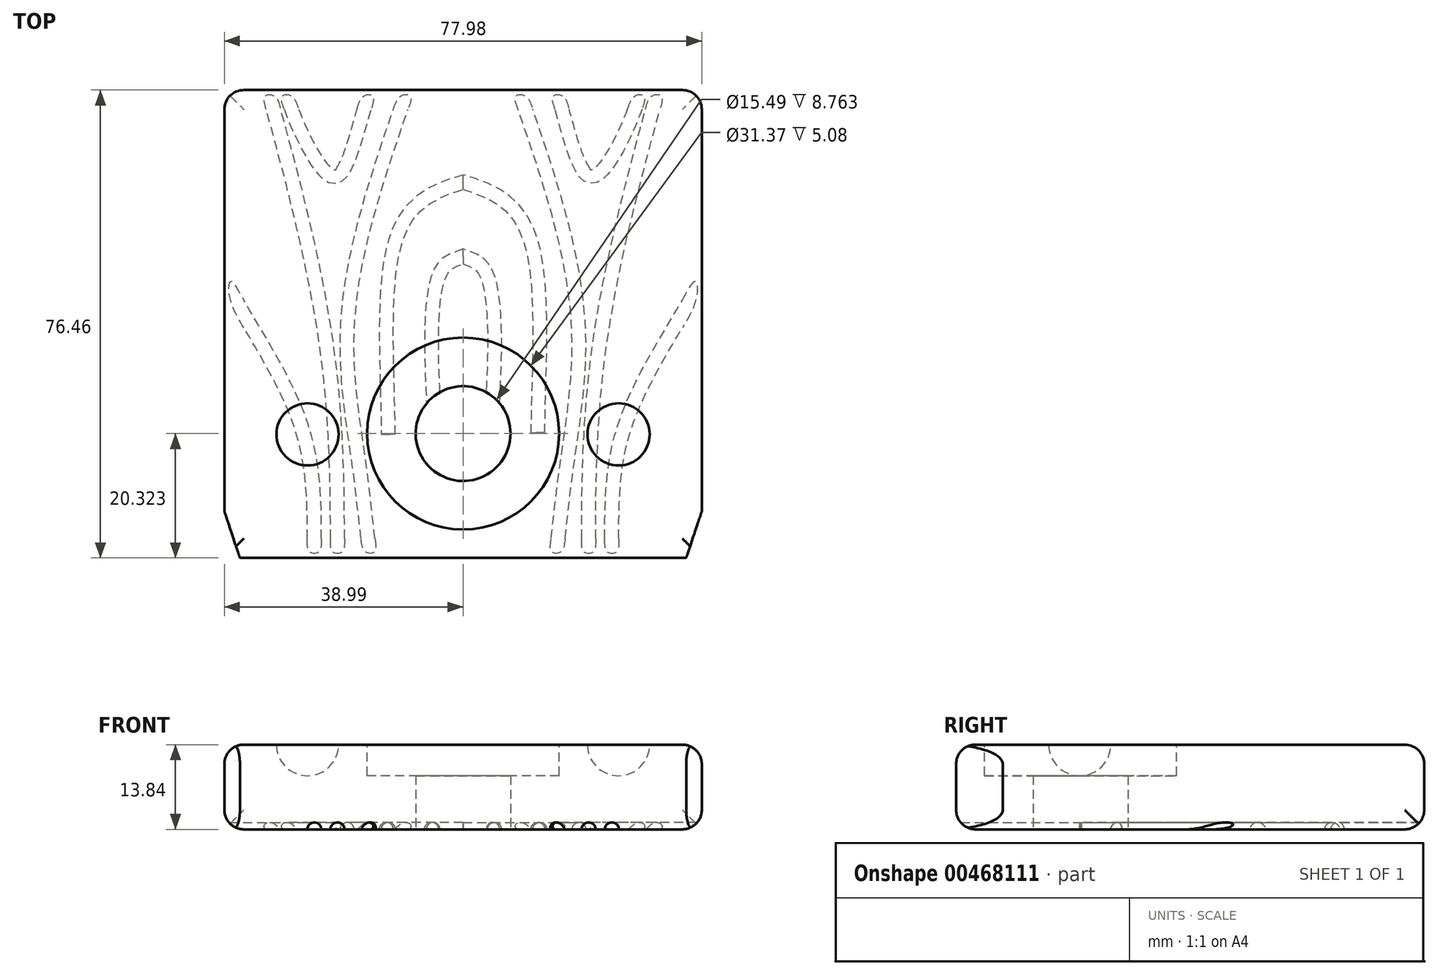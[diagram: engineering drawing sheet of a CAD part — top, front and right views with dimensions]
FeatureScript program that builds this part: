
annotation { "Feature Type Name" : "Feature", "Feature Type Description" : "" }
export const myFeature = defineFeature(function(context is Context, id is Id, definition is map)
    precondition{}
    {
        {
            var Q0;
            Q0=qCreatedBy(makeId("Top.planeOp"),FACE);
            var sketch = newSketch(context, id + "F0", { "sketchPlane" : qUnion([Q0])});
            skLineSegment(sketch, "E0.bottom", {"start": v(38.99, 38.23) * mm, "end": v(-38.99, 38.23) * mm});
            skLineSegment(sketch, "E0.top", {"start": v(38.99, -38.23) * mm, "end": v(-38.99, -38.23) * mm});
            skLineSegment(sketch, "E0.left", {"start": v(38.99, 38.23) * mm, "end": v(38.99, -38.23) * mm});
            skLineSegment(sketch, "E0.right", {"start": v(-38.99, 38.23) * mm, "end": v(-38.99, -38.23) * mm});
            skPoint(sketch, "E0.middle", {"position": v(0, 0) * mm});
            skCircle(sketch, "E1", {"center": v(0, -17.9) * mm, "radius": 7.75 * mm});
            skSolve(sketch);
        }
        {
            var Q0;
            Q0=makeQuery(id+"F0.imprint","IMPRINT",FACE,{"disambiguationData":[TD([[makeQuery(id+"F0.imprint","IMPRINT",EDGE,{"derivedFrom":sQuery(id+"F0.wireOp",EDGE,"E0.bottom")}),1.0]])]});
            extrude(context, id + "F1", {"entities" : qUnion([Q0]), "depth" : 13.84 * mm});
        }
        {
            var Q0;
            Q0=makeQuery(id+"F1.opExtrude","CAP_FACE",FACE,{"disambiguationData":[OSD([sQuery(id+"F0.wireOp",EDGE,"E0.bottom"),sQuery(id+"F0.wireOp",EDGE,"E0.top"),sQuery(id+"F0.wireOp",EDGE,"E0.left"),sQuery(id+"F0.wireOp",EDGE,"E0.right"),sQuery(id+"F0.wireOp",EDGE,"E1")])],"isStart":false});
            var sketch = newSketch(context, id + "F2", { "sketchPlane" : qUnion([Q0])});
            skCircle(sketch, "E2.0", {"center": v(0, -17.9) * mm, "radius": 7.75 * mm});
            skCircle(sketch, "E3", {"center": v(0, -17.9) * mm, "radius": 15.68 * mm});
            skSolve(sketch);
        }
        {
            var Q0;
            Q0=makeQuery(id+"F2.imprint","IMPRINT",FACE,{"disambiguationData":[TD([[makeQuery(id+"F2.imprint","IMPRINT",EDGE,{"derivedFrom":sQuery(id+"F2.wireOp",EDGE,"E2.0")}),-1.0]])]});
            extrude(context, id + "F3", {"entities" : qUnion([Q0]), "operationType" : NewBodyOperationType.REMOVE, "oppositeDirection" : true, "depth" : 5.08 * mm});
        }
        {
            var Q0;
            Q0=qCreatedBy(makeId("Front.planeOp"),FACE);
            cPlane(context, id + "F4", {"entities" : qUnion([Q0]), "cplaneType" : CPlaneType.OFFSET, "offset" : 18.03 * mm, "width" : 152.4 * mm, "height" : 152.4 * mm});
        }
        {
            var Q0;
            Q0=qCreatedBy(id+"F4.planeOp",FACE);
            var sketch = newSketch(context, id + "F5", { "sketchPlane" : qUnion([Q0])});
            skLineSegment(sketch, "E4.0", {"start": v(38.99, 13.84) * mm, "end": v(-38.99, 13.84) * mm});
            skArc(sketch, "E5", {"start": v(-30.48, 13.84) * mm, "mid": v(-25.4, 8.76) * mm, "end": v(-20.32, 13.84) * mm});
            skArc(sketch, "E6.MirrorCS", {"start": v(30.48, 13.84) * mm, "mid": v(25.4, 8.76) * mm, "end": v(20.32, 13.84) * mm});
            skSolve(sketch);
        }
        {
            var Q0;
            Q0 = qSketchRegion(id + "F5", true);
            var Q1;
            Q1=sQuery(id+"F5.wireOp",EDGE,"E4.0");
            revolve(context, id + "F6", {"operationType" : NewBodyOperationType.REMOVE, "entities" : qUnion([Q0]), "axis" : qUnion([Q1]), "revolveType" : RevolveType.FULL, "oppositeDirection" : true});
        }
        {
            var Q0;
            Q0=makeQuery(id+"F1.opExtrude","SWEPT_EDGE",EDGE,{"disambiguationData":[OSD([sQuery(id+"F0.wireOp",EDGE,"E0.top"),sQuery(id+"F0.wireOp",EDGE,"E0.right")])]});
            var Q1;
            Q1=makeQuery(id+"F1.opExtrude","SWEPT_EDGE",EDGE,{"disambiguationData":[OSD([sQuery(id+"F0.wireOp",EDGE,"E0.top"),sQuery(id+"F0.wireOp",EDGE,"E0.left")])]});
            chamfer(context, id + "F7", {"entities" : qUnion([Q0, Q1]), "chamferType" : ChamferType.TWO_OFFSETS, "width1" : 2.54 * mm, "oppositeDirection" : false, "width2" : 7.62 * mm});
        }
        {
            var Q0;
            Q0=qCreatedBy(makeId("Top.planeOp"),FACE);
            var sketch = newSketch(context, id + "F8", { "sketchPlane" : qUnion([Q0])});
            skPoint(sketch, "E7.0", {"position": v(-35.81, 0) * mm});
            skFitSpline(sketch, "E8", {"points": [v(39.06, 7.42) * mm, v(26.22, -17.3) * mm, v(24.29, -38.04) * mm], "startDerivative": vector(-21.66, -42.08) * mm, "endDerivative": vector(-0.35, -37.77) * mm});
            skFitSpline(sketch, "E9", {"points": [v(31.84, 38.23) * mm, v(22.23, -3.88) * mm, v(20.51, -38.04) * mm], "startDerivative": vector(-20.67, -75.16) * mm, "endDerivative": vector(0.12, -64.83) * mm});
            skFitSpline(sketch, "E10", {"points": [v(29, 38.23) * mm, v(24.75, 28) * mm, v(20.51, 24.22) * mm, v(15.1, 38.57) * mm], "startDerivative": vector(-5.15, -22.25) * mm, "endDerivative": vector(-13.12, 38.58) * mm});
            skFitSpline(sketch, "E11", {"points": [v(9.07, 38.17) * mm, v(18.67, 2.2) * mm, v(16.88, -23.38) * mm, v(15.1, -38.04) * mm], "startDerivative": vector(28.46, -81.14) * mm, "endDerivative": vector(-6.65, -43.93) * mm});
            skFitSpline(sketch, "E12", {"points": [v(12.22, -17.9) * mm, v(11.95, 9.33) * mm, v(7.13, 19.82) * mm, v(0, 23.17) * mm], "startDerivative": vector(-0.09, 43.18) * mm, "endDerivative": vector(-28.23, 8.15) * mm});
            skFitSpline(sketch, "E13", {"points": [v(4.57, -17.9) * mm, v(3.78, 8.28) * mm, v(0, 11.01) * mm], "startDerivative": vector(0.77, 22.83) * mm, "endDerivative": vector(-11.34, 4.74) * mm});
            skFitSpline(sketch, "E14.MirrorCS", {"points": [v(-4.57, -17.9) * mm, v(-3.78, 8.28) * mm, v(0, 11.01) * mm], "startDerivative": vector(-0.77, 22.83) * mm, "endDerivative": vector(11.34, 4.74) * mm});
            skFitSpline(sketch, "E15.MirrorCS", {"points": [v(-12.22, -17.9) * mm, v(-11.95, 9.33) * mm, v(-7.13, 19.82) * mm, v(0, 23.17) * mm], "startDerivative": vector(0.09, 43.18) * mm, "endDerivative": vector(28.23, 8.15) * mm});
            skFitSpline(sketch, "E16.MirrorCS", {"points": [v(-9.07, 38.17) * mm, v(-18.67, 2.2) * mm, v(-16.88, -23.38) * mm, v(-15.1, -38.04) * mm], "startDerivative": vector(-28.46, -81.14) * mm, "endDerivative": vector(6.65, -43.93) * mm});
            skFitSpline(sketch, "E17.MirrorCS", {"points": [v(-29, 38.23) * mm, v(-24.75, 28) * mm, v(-20.51, 24.22) * mm, v(-15.1, 38.57) * mm], "startDerivative": vector(5.15, -22.25) * mm, "endDerivative": vector(13.12, 38.58) * mm});
            skFitSpline(sketch, "E18.MirrorCS", {"points": [v(-31.84, 38.23) * mm, v(-22.23, -3.88) * mm, v(-20.51, -38.04) * mm], "startDerivative": vector(20.67, -75.16) * mm, "endDerivative": vector(-0.12, -64.83) * mm});
            skFitSpline(sketch, "E19.MirrorCS", {"points": [v(-39.06, 7.42) * mm, v(-26.22, -17.3) * mm, v(-24.29, -38.04) * mm], "startDerivative": vector(21.66, -42.08) * mm, "endDerivative": vector(0.35, -37.77) * mm});
            skLineSegment(sketch, "E20.0", {"start": v(38.99, 38.23) * mm, "end": v(-38.99, 38.23) * mm});
            skLineSegment(sketch, "E21.0", {"start": v(38.99, 38.23) * mm, "end": v(38.99, -30.6) * mm});
            skLineSegment(sketch, "E22.0", {"start": v(-38.99, 38.23) * mm, "end": v(-38.99, -30.6) * mm});
            skLineSegment(sketch, "E23.0", {"start": v(36.45, -38.23) * mm, "end": v(-36.45, -38.23) * mm});
            skCircle(sketch, "E24.0", {"center": v(0, -17.9) * mm, "radius": 7.75 * mm});
            skLineSegment(sketch, "E25", {"start": v(48.87, -17.9) * mm, "end": v(-50.84, -17.9) * mm, "construction": true});
            skLineSegment(sketch, "E26.0.2", {"start": v(-38.99, 38.23) * mm, "end": v(38.99, 38.23) * mm});
            skLineSegment(sketch, "E27", {"start": v(-37.89, 38.23) * mm, "end": v(38.99, 38.23) * mm});
            skSolve(sketch);
        }
        {
            var Q0;
            Q0=makeQuery(id+"F1.opExtrude","SWEPT_FACE",FACE,{"disambiguationData":[OSD([sQuery(id+"F0.wireOp",EDGE,"E0.top")])]});
            var sketch = newSketch(context, id + "F9", { "sketchPlane" : qUnion([Q0])});
            skPoint(sketch, "E28.0", {"position": v(24.29, 0) * mm});
            skPoint(sketch, "E29.0", {"position": v(15.1, 0) * mm});
            skPoint(sketch, "E30.0", {"position": v(-15.1, 0) * mm});
            skPoint(sketch, "E31.0", {"position": v(-20.51, 0) * mm});
            skPoint(sketch, "E32.0", {"position": v(-24.29, 0) * mm});
            skPoint(sketch, "E33.0", {"position": v(20.51, 0) * mm});
            skCircle(sketch, "E34", {"center": v(24.29, 0) * mm, "radius": 1.14 * mm});
            skCircle(sketch, "E35", {"center": v(20.51, 0) * mm, "radius": 1.14 * mm});
            skCircle(sketch, "E36", {"center": v(15.1, 0) * mm, "radius": 1.14 * mm});
            skCircle(sketch, "E37", {"center": v(-15.1, 0) * mm, "radius": 1.14 * mm});
            skCircle(sketch, "E38", {"center": v(-20.51, 0) * mm, "radius": 1.14 * mm});
            skCircle(sketch, "E39", {"center": v(-24.29, 0) * mm, "radius": 1.14 * mm});
            skSolve(sketch);
        }
        {
            var Q0;
            {var subQ0=sQuery(id+"F9.wireOp",EDGE,"E34");var subQ1=makeQuery(id+"F1.opExtrude","CAP_EDGE",EDGE,{"disambiguationData":[OSD([sQuery(id+"F0.wireOp",EDGE,"E0.top")])],"isStart":true});var subQ2=makeQuery(id+"F9.imprint","INTERSECT",VERTEX,{"disambiguationData":[OD(0.0)],"derivedFrom":[subQ1,subQ0]});Q0=makeQuery(id+"F9.imprint","IMPRINT",FACE,{"disambiguationData":[TD([[makeQuery(id+"F9.imprint","IMPRINT",EDGE,{"disambiguationData":[TD([[subQ2,-1.0]])],"derivedFrom":subQ0}),1.0]])]});}
            var Q1;
            Q1=sQuery(id+"F8.wireOp",EDGE,"E8");
            sweep(context, id + "F10", {"operationType" : NewBodyOperationType.REMOVE, "profiles" : qUnion([Q0]), "path" : qUnion([Q1])});
        }
        {
            var Q0;
            {var subQ0=sQuery(id+"F9.wireOp",EDGE,"E35");var subQ1=makeQuery(id+"F1.opExtrude","CAP_EDGE",EDGE,{"disambiguationData":[OSD([sQuery(id+"F0.wireOp",EDGE,"E0.top")])],"isStart":true});var subQ2=makeQuery(id+"F9.imprint","INTERSECT",VERTEX,{"disambiguationData":[OD(0.0)],"derivedFrom":[subQ1,subQ0]});Q0=makeQuery(id+"F9.imprint","IMPRINT",FACE,{"disambiguationData":[TD([[makeQuery(id+"F9.imprint","IMPRINT",EDGE,{"disambiguationData":[TD([[subQ2,-1.0]])],"derivedFrom":subQ0}),1.0]])]});}
            var Q1;
            Q1=sQuery(id+"F8.wireOp",EDGE,"E9");
            sweep(context, id + "F11", {"operationType" : NewBodyOperationType.REMOVE, "profiles" : qUnion([Q0]), "path" : qUnion([Q1])});
        }
        {
            var Q0;
            {var subQ0=sQuery(id+"F9.wireOp",EDGE,"E36");var subQ1=makeQuery(id+"F1.opExtrude","CAP_EDGE",EDGE,{"disambiguationData":[OSD([sQuery(id+"F0.wireOp",EDGE,"E0.top")])],"isStart":true});var subQ2=makeQuery(id+"F9.imprint","INTERSECT",VERTEX,{"disambiguationData":[OD(0.0)],"derivedFrom":[subQ1,subQ0]});Q0=makeQuery(id+"F9.imprint","IMPRINT",FACE,{"disambiguationData":[TD([[makeQuery(id+"F9.imprint","IMPRINT",EDGE,{"disambiguationData":[TD([[subQ2,-1.0]])],"derivedFrom":subQ0}),1.0]])]});}
            var Q1;
            Q1=sQuery(id+"F8.wireOp",EDGE,"E11");
            sweep(context, id + "F12", {"operationType" : NewBodyOperationType.REMOVE, "profiles" : qUnion([Q0]), "path" : qUnion([Q1])});
        }
        {
            var Q0;
            {var subQ0=sQuery(id+"F9.wireOp",EDGE,"E37");var subQ1=makeQuery(id+"F1.opExtrude","CAP_EDGE",EDGE,{"disambiguationData":[OSD([sQuery(id+"F0.wireOp",EDGE,"E0.top")])],"isStart":true});var subQ2=makeQuery(id+"F9.imprint","INTERSECT",VERTEX,{"disambiguationData":[OD(0.0)],"derivedFrom":[subQ1,subQ0]});Q0=makeQuery(id+"F9.imprint","IMPRINT",FACE,{"disambiguationData":[TD([[makeQuery(id+"F9.imprint","IMPRINT",EDGE,{"disambiguationData":[TD([[subQ2,1.0]])],"derivedFrom":subQ0}),1.0]])]});}
            var Q1;
            Q1=sQuery(id+"F8.wireOp",EDGE,"E16.MirrorCS");
            sweep(context, id + "F13", {"operationType" : NewBodyOperationType.REMOVE, "profiles" : qUnion([Q0]), "path" : qUnion([Q1])});
        }
        {
            var Q0;
            {var subQ0=sQuery(id+"F9.wireOp",EDGE,"E38");var subQ1=makeQuery(id+"F1.opExtrude","CAP_EDGE",EDGE,{"disambiguationData":[OSD([sQuery(id+"F0.wireOp",EDGE,"E0.top")])],"isStart":true});var subQ2=makeQuery(id+"F9.imprint","INTERSECT",VERTEX,{"disambiguationData":[OD(0.0)],"derivedFrom":[subQ1,subQ0]});Q0=makeQuery(id+"F9.imprint","IMPRINT",FACE,{"disambiguationData":[TD([[makeQuery(id+"F9.imprint","IMPRINT",EDGE,{"disambiguationData":[TD([[subQ2,1.0]])],"derivedFrom":subQ0}),1.0]])]});}
            var Q1;
            Q1=sQuery(id+"F8.wireOp",EDGE,"E18.MirrorCS");
            sweep(context, id + "F14", {"operationType" : NewBodyOperationType.REMOVE, "profiles" : qUnion([Q0]), "path" : qUnion([Q1])});
        }
        {
            var Q0;
            {var subQ0=sQuery(id+"F9.wireOp",EDGE,"E39");var subQ1=makeQuery(id+"F1.opExtrude","CAP_EDGE",EDGE,{"disambiguationData":[OSD([sQuery(id+"F0.wireOp",EDGE,"E0.top")])],"isStart":true});var subQ2=makeQuery(id+"F9.imprint","INTERSECT",VERTEX,{"disambiguationData":[OD(0.0)],"derivedFrom":[subQ1,subQ0]});Q0=makeQuery(id+"F9.imprint","IMPRINT",FACE,{"disambiguationData":[TD([[makeQuery(id+"F9.imprint","IMPRINT",EDGE,{"disambiguationData":[TD([[subQ2,1.0]])],"derivedFrom":subQ0}),1.0]])]});}
            var Q1;
            Q1=sQuery(id+"F8.wireOp",EDGE,"E19.MirrorCS");
            sweep(context, id + "F15", {"operationType" : NewBodyOperationType.REMOVE, "profiles" : qUnion([Q0]), "path" : qUnion([Q1])});
        }
        {
            var Q0;
            Q0=makeQuery(id+"F1.opExtrude","SWEPT_FACE",FACE,{"disambiguationData":[OSD([sQuery(id+"F0.wireOp",EDGE,"E0.bottom")])]});
            var sketch = newSketch(context, id + "F16", { "sketchPlane" : qUnion([Q0])});
            skPoint(sketch, "E40.0", {"position": v(15.22, 0) * mm});
            skPoint(sketch, "E41.0", {"position": v(-15.1, 0) * mm});
            skCircle(sketch, "E42", {"center": v(15.22, 0) * mm, "radius": 1.14 * mm});
            skCircle(sketch, "E43", {"center": v(-15.1, 0) * mm, "radius": 1.14 * mm});
            skPoint(sketch, "E44.0", {"position": v(29, 0) * mm});
            skPoint(sketch, "E45.0", {"position": v(-29, 0) * mm});
            skCircle(sketch, "E46", {"center": v(-29, 0) * mm, "radius": 1.14 * mm});
            skCircle(sketch, "E47", {"center": v(29, 0) * mm, "radius": 1.14 * mm});
            skSolve(sketch);
        }
        {
            var Q0;
            {var subQ0=sQuery(id+"F16.wireOp",EDGE,"E47");var subQ1=sQuery(id+"F0.wireOp",EDGE,"E0.bottom");var subQ3=sQuery(id+"F0.wireOp",EDGE,"E0.right");var subQ6=makeQuery(id+"F13.opSweep","SWEPT_FACE",FACE,{"disambiguationData":[OSD([sQuery(id+"F8.wireOp",EDGE,"E16.MirrorCS"),sQuery(id+"F9.wireOp",EDGE,"E37")])]});var subQ7=makeQuery(id+"F1.opExtrude","SWEPT_FACE",FACE,{"disambiguationData":[OSD([subQ3])]});var subQ8=makeQuery(id+"F14.boolean.opBoolean","SPLIT",EDGE,{"disambiguationData":[TD([makeQuery(id+"F13.boolean.opBoolean","COPY",FACE,{"derivedFrom":subQ6})])],"derivedFrom":makeQuery(id+"F13.boolean.opBoolean","SPLIT",EDGE,{"disambiguationData":[TD([subQ7])],"derivedFrom":makeQuery(id+"F12.boolean.opBoolean","SPLIT",EDGE,{"disambiguationData":[TD([subQ7])],"derivedFrom":makeQuery(id+"F11.boolean.opBoolean","SPLIT",EDGE,{"disambiguationData":[TD([subQ7])],"derivedFrom":makeQuery(id+"F1.opExtrude","CAP_EDGE",EDGE,{"disambiguationData":[OSD([subQ1])],"isStart":true})})})})});var subQ9=makeQuery(id+"F16.imprint","INTERSECT",VERTEX,{"disambiguationData":[OD(0.0)],"derivedFrom":[subQ8,subQ0]});Q0=makeQuery(id+"F16.imprint","IMPRINT",FACE,{"disambiguationData":[TD([[makeQuery(id+"F16.imprint","IMPRINT",EDGE,{"disambiguationData":[TD([[subQ9,-1.0]])],"derivedFrom":subQ0}),1.0]])]});}
            var Q1;
            Q1=sQuery(id+"F8.wireOp",EDGE,"E17.MirrorCS");
            sweep(context, id + "F17", {"operationType" : NewBodyOperationType.REMOVE, "profiles" : qUnion([Q0]), "path" : qUnion([Q1])});
        }
        {
            var Q0;
            {var subQ0=sQuery(id+"F16.wireOp",EDGE,"E46");var subQ1=sQuery(id+"F0.wireOp",EDGE,"E0.bottom");var subQ3=sQuery(id+"F0.wireOp",EDGE,"E0.right");var subQ5=makeQuery(id+"F11.opSweep","SWEPT_FACE",FACE,{"disambiguationData":[OSD([sQuery(id+"F8.wireOp",EDGE,"E9"),sQuery(id+"F9.wireOp",EDGE,"E35")])]});var subQ6=makeQuery(id+"F12.boolean.opBoolean","SPLIT",EDGE,{"disambiguationData":[TD([makeQuery(id+"F11.boolean.opBoolean","COPY",FACE,{"derivedFrom":subQ5})])],"derivedFrom":makeQuery(id+"F11.boolean.opBoolean","SPLIT",EDGE,{"disambiguationData":[TD([makeQuery(id+"F1.opExtrude","SWEPT_FACE",FACE,{"disambiguationData":[OSD([subQ3])]})])],"derivedFrom":makeQuery(id+"F1.opExtrude","CAP_EDGE",EDGE,{"disambiguationData":[OSD([subQ1])],"isStart":true})})});var subQ7=makeQuery(id+"F16.imprint","INTERSECT",VERTEX,{"disambiguationData":[OD(0.0)],"derivedFrom":[subQ6,subQ0]});Q0=makeQuery(id+"F16.imprint","IMPRINT",FACE,{"disambiguationData":[TD([[makeQuery(id+"F16.imprint","IMPRINT",EDGE,{"disambiguationData":[TD([[subQ7,1.0]])],"derivedFrom":subQ0}),1.0]])]});}
            var Q1;
            Q1=sQuery(id+"F8.wireOp",EDGE,"E10");
            sweep(context, id + "F18", {"operationType" : NewBodyOperationType.REMOVE, "profiles" : qUnion([Q0]), "path" : qUnion([Q1])});
        }
        {
            var Q0;
            Q0=qCreatedBy(id+"F4.planeOp",FACE);
            var sketch = newSketch(context, id + "F19", { "sketchPlane" : qUnion([Q0])});
            skCircle(sketch, "E48", {"center": v(-12.22, 0) * mm, "radius": 1.14 * mm});
            skCircle(sketch, "E49", {"center": v(-4.58, 0) * mm, "radius": 1.14 * mm});
            skSolve(sketch);
        }
        {
            var Q0;
            Q0=makeQuery(id+"F19.imprint","IMPRINT",FACE,{"disambiguationData":[TD([[makeQuery(id+"F19.imprint","IMPRINT",EDGE,{"derivedFrom":sQuery(id+"F19.wireOp",EDGE,"E48")}),1.0]])]});
            var Q1;
            Q1=sQuery(id+"F8.wireOp",EDGE,"E15.MirrorCS");
            var Q2;
            Q2=sQuery(id+"F8.wireOp",EDGE,"E12");
            sweep(context, id + "F20", {"operationType" : NewBodyOperationType.REMOVE, "profiles" : qUnion([Q0]), "path" : qUnion([Q1, Q2])});
        }
        {
            var Q0;
            Q0=makeQuery(id+"F19.imprint","IMPRINT",FACE,{"disambiguationData":[TD([[makeQuery(id+"F19.imprint","IMPRINT",EDGE,{"derivedFrom":sQuery(id+"F19.wireOp",EDGE,"E49")}),1.0]])]});
            var Q1;
            Q1=sQuery(id+"F8.wireOp",EDGE,"E14.MirrorCS");
            var Q2;
            Q2=sQuery(id+"F8.wireOp",EDGE,"E13");
            sweep(context, id + "F21", {"operationType" : NewBodyOperationType.REMOVE, "profiles" : qUnion([Q0]), "path" : qUnion([Q1, Q2])});
        }
        {
            var Q0;
            Q0=qCreatedBy(makeId("Top.planeOp"),FACE);
            cPlane(context, id + "F22", {"entities" : qUnion([Q0]), "cplaneType" : CPlaneType.OFFSET, "offset" : 6.92 * mm, "width" : 152.4 * mm, "height" : 152.4 * mm});
        }
        {
            var Q0;
            {var subQ0=sQuery(id+"F0.wireOp",EDGE,"E0.right");var subQ1=sQuery(id+"F0.wireOp",EDGE,"E0.top");var subQ4=makeQuery(id+"FcEpPnPIbSgFIcs_1.1.F12.opSweep","SWEPT_FACE",FACE,{"disambiguationData":[OSD([sQuery(id+"F8.wireOp",EDGE,"E11"),sQuery(id+"F9.wireOp",EDGE,"E36")])]});var subQ5=makeQuery(id+"F7.opChamfer","BLEND_FACE",FACE,{"disambiguationData":[OSD([subQ1,subQ0])]});Q0=makeQuery(id+"FcEpPnPIbSgFIcs_1.1.F13.boolean.opBoolean","SPLIT",EDGE,{"disambiguationData":[TD([makeQuery(id+"FcEpPnPIbSgFIcs_1.1.F12.boolean.opBoolean","COPY",FACE,{"derivedFrom":subQ4})])],"derivedFrom":makeQuery(id+"FcEpPnPIbSgFIcs_1.1.F12.boolean.opBoolean","SPLIT",EDGE,{"disambiguationData":[TD([subQ5])],"derivedFrom":makeQuery(id+"FcEpPnPIbSgFIcs_1.1.F11.boolean.opBoolean","SPLIT",EDGE,{"disambiguationData":[TD([subQ5])],"derivedFrom":makeQuery(id+"FcEpPnPIbSgFIcs_1.1.F10.boolean.opBoolean","SPLIT",EDGE,{"disambiguationData":[TD([subQ5])],"derivedFrom":makeQuery(id+"F1.opExtrude","CAP_EDGE",EDGE,{"disambiguationData":[OSD([subQ1])],"isStart":false})})})})});}
            var Q1;
            {var subQ0=sQuery(id+"F0.wireOp",EDGE,"E0.right");var subQ1=sQuery(id+"F0.wireOp",EDGE,"E0.top");var subQ3=makeQuery(id+"F12.opSweep","SWEPT_FACE",FACE,{"disambiguationData":[OSD([sQuery(id+"F8.wireOp",EDGE,"E11"),sQuery(id+"F9.wireOp",EDGE,"E36")])]});var subQ5=makeQuery(id+"F7.opChamfer","BLEND_FACE",FACE,{"disambiguationData":[OSD([subQ1,subQ0])]});Q1=makeQuery(id+"F13.boolean.opBoolean","SPLIT",EDGE,{"disambiguationData":[TD([makeQuery(id+"F12.boolean.opBoolean","COPY",FACE,{"derivedFrom":subQ3})])],"derivedFrom":makeQuery(id+"F12.boolean.opBoolean","SPLIT",EDGE,{"disambiguationData":[TD([subQ5])],"derivedFrom":makeQuery(id+"F11.boolean.opBoolean","SPLIT",EDGE,{"disambiguationData":[TD([subQ5])],"derivedFrom":makeQuery(id+"F10.boolean.opBoolean","SPLIT",EDGE,{"disambiguationData":[TD([subQ5])],"derivedFrom":makeQuery(id+"F1.opExtrude","CAP_EDGE",EDGE,{"disambiguationData":[OSD([subQ1])],"isStart":true})})})})});}
            var Q2;
            Q2=makeQuery(id+"F1.opExtrude","SWEPT_EDGE",EDGE,{"disambiguationData":[OSD([sQuery(id+"F0.wireOp",EDGE,"E0.bottom"),sQuery(id+"F0.wireOp",EDGE,"E0.left")])]});
            var Q3;
            Q3=makeQuery(id+"F1.opExtrude","SWEPT_EDGE",EDGE,{"disambiguationData":[OSD([sQuery(id+"F0.wireOp",EDGE,"E0.bottom"),sQuery(id+"F0.wireOp",EDGE,"E0.right")])]});
            var Q4;
            {var subQ0=sQuery(id+"F0.wireOp",EDGE,"E0.bottom");var subQ2=sQuery(id+"F0.wireOp",EDGE,"E0.left");Q4=makeQuery(id+"FcEpPnPIbSgFIcs_1.1.F10.boolean.opBoolean","SPLIT",EDGE,{"disambiguationData":[TD([makeQuery(id+"F1.opExtrude","SWEPT_FACE",FACE,{"disambiguationData":[OSD([subQ0])]})])],"derivedFrom":makeQuery(id+"F1.opExtrude","CAP_EDGE",EDGE,{"disambiguationData":[OSD([subQ2])],"isStart":false})});}
            var Q5;
            {var subQ0=sQuery(id+"F0.wireOp",EDGE,"E0.bottom");var subQ1=sQuery(id+"F0.wireOp",EDGE,"E0.right");Q5=makeQuery(id+"FcEpPnPIbSgFIcs_1.1.F15.boolean.opBoolean","SPLIT",EDGE,{"disambiguationData":[TD([makeQuery(id+"F1.opExtrude","SWEPT_FACE",FACE,{"disambiguationData":[OSD([subQ0])]})])],"derivedFrom":makeQuery(id+"F1.opExtrude","CAP_EDGE",EDGE,{"disambiguationData":[OSD([subQ1])],"isStart":false})});}
            var Q6;
            {var subQ0=sQuery(id+"F0.wireOp",EDGE,"E0.bottom");var subQ2=sQuery(id+"F0.wireOp",EDGE,"E0.left");Q6=makeQuery(id+"F10.boolean.opBoolean","SPLIT",EDGE,{"disambiguationData":[TD([makeQuery(id+"F1.opExtrude","SWEPT_FACE",FACE,{"disambiguationData":[OSD([subQ0])]})])],"derivedFrom":makeQuery(id+"F1.opExtrude","CAP_EDGE",EDGE,{"disambiguationData":[OSD([subQ2])],"isStart":true})});}
            var Q7;
            {var subQ0=sQuery(id+"F0.wireOp",EDGE,"E0.bottom");var subQ1=sQuery(id+"F0.wireOp",EDGE,"E0.right");Q7=makeQuery(id+"F15.boolean.opBoolean","SPLIT",EDGE,{"disambiguationData":[TD([makeQuery(id+"F1.opExtrude","SWEPT_FACE",FACE,{"disambiguationData":[OSD([subQ0])]})])],"derivedFrom":makeQuery(id+"F1.opExtrude","CAP_EDGE",EDGE,{"disambiguationData":[OSD([subQ1])],"isStart":true})});}
            fillet(context, id + "F23", {"entities" : qUnion([Q0, Q1, Q2, Q3, Q4, Q5, Q6, Q7]), "radius" : 3.17 * mm, "allowEdgeOverflow" : false});
        }
        {
            var Q0;
            {var subQ0=sQuery(id+"F0.wireOp",EDGE,"E0.bottom");var subQ2=sQuery(id+"F0.wireOp",EDGE,"E0.right");var subQ3=sQuery(id+"F0.wireOp",EDGE,"E0.top");var subQ5=makeQuery(id+"FcEpPnPIbSgFIcs_1.1.F12.opSweep","CAP_FACE",FACE,{"disambiguationData":[OSD([subQ3,sQuery(id+"F8.wireOp",VERTEX,"E11.start"),sQuery(id+"F9.wireOp",EDGE,"E36")])],"isStart":false});var subQ6=makeQuery(id+"F1.opExtrude","SWEPT_FACE",FACE,{"disambiguationData":[OSD([subQ2])]});Q0=makeQuery(id+"FcEpPnPIbSgFIcs_1.1.F13.boolean.opBoolean","SPLIT",EDGE,{"disambiguationData":[TD([makeQuery(id+"FcEpPnPIbSgFIcs_1.1.F12.boolean.opBoolean","COPY",FACE,{"derivedFrom":subQ5})])],"derivedFrom":makeQuery(id+"FcEpPnPIbSgFIcs_1.1.F12.boolean.opBoolean","SPLIT",EDGE,{"disambiguationData":[TD([subQ6])],"derivedFrom":makeQuery(id+"FcEpPnPIbSgFIcs_1.1.F11.boolean.opBoolean","SPLIT",EDGE,{"disambiguationData":[TD([subQ6])],"derivedFrom":makeQuery(id+"F1.opExtrude","CAP_EDGE",EDGE,{"disambiguationData":[OSD([subQ0])],"isStart":false})})})});}
            var Q1;
            {var subQ0=sQuery(id+"F0.wireOp",EDGE,"E0.bottom");var subQ2=sQuery(id+"F0.wireOp",EDGE,"E0.top");var subQ3=makeQuery(id+"F12.opSweep","CAP_FACE",FACE,{"disambiguationData":[OSD([subQ2,sQuery(id+"F8.wireOp",VERTEX,"E11.start"),sQuery(id+"F9.wireOp",EDGE,"E36")])],"isStart":false});var subQ4=sQuery(id+"F0.wireOp",EDGE,"E0.right");var subQ6=makeQuery(id+"F1.opExtrude","SWEPT_FACE",FACE,{"disambiguationData":[OSD([subQ4])]});Q1=makeQuery(id+"F13.boolean.opBoolean","SPLIT",EDGE,{"disambiguationData":[TD([makeQuery(id+"F12.boolean.opBoolean","COPY",FACE,{"derivedFrom":subQ3})])],"derivedFrom":makeQuery(id+"F12.boolean.opBoolean","SPLIT",EDGE,{"disambiguationData":[TD([subQ6])],"derivedFrom":makeQuery(id+"F11.boolean.opBoolean","SPLIT",EDGE,{"disambiguationData":[TD([subQ6])],"derivedFrom":makeQuery(id+"F1.opExtrude","CAP_EDGE",EDGE,{"disambiguationData":[OSD([subQ0])],"isStart":true})})})});}
            fillet(context, id + "F24", {"entities" : qUnion([Q0, Q1]), "radius" : 3.17 * mm, "tangentPropagation" : true, "allowEdgeOverflow" : false});
        }
    });
